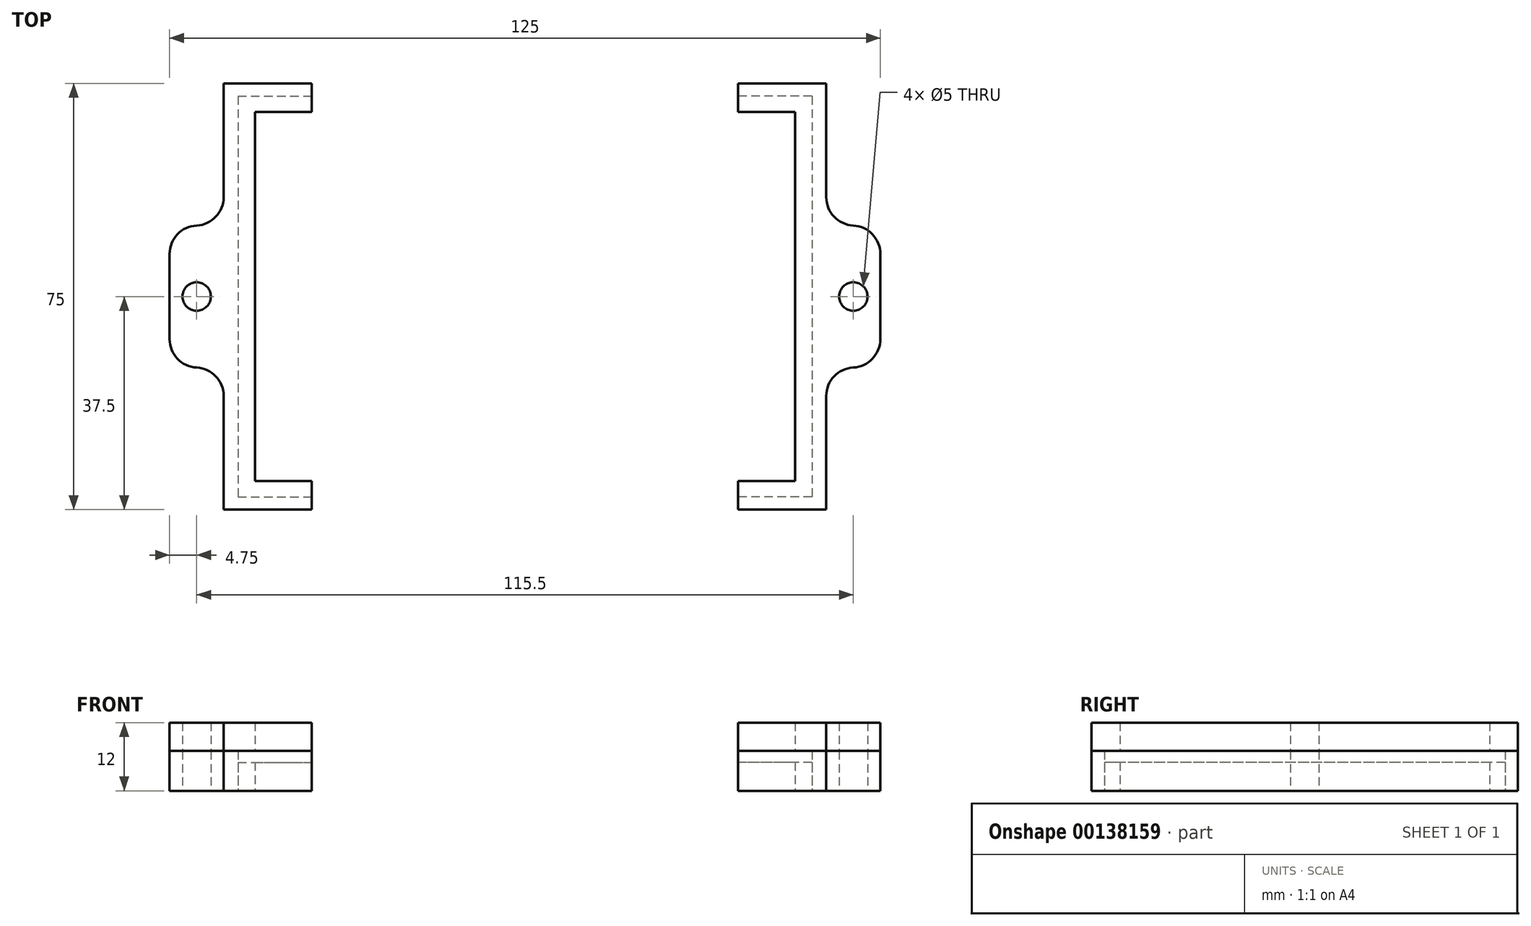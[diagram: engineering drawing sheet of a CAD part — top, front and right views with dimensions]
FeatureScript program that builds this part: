
annotation { "Feature Type Name" : "Feature", "Feature Type Description" : "" }
export const myFeature = defineFeature(function(context is Context, id is Id, definition is map)
    precondition{}
    {
        {
            var Q0;
            Q0=qCreatedBy(makeId("Top.planeOp"),FACE);
            var sketch = newSketch(context, id + "F0", { "sketchPlane" : qUnion([Q0])});
            skLineSegment(sketch, "E0.left", {"start": v(-50.5, 35.25) * mm, "end": v(-50.5, -35.25) * mm});
            skLineSegment(sketch, "E0.right", {"start": v(50.5, 35.25) * mm, "end": v(50.5, -35.25) * mm});
            skPoint(sketch, "E0.middle", {"position": v(0, 0) * mm});
            skLineSegment(sketch, "E1.left", {"start": v(-47.5, 32.5) * mm, "end": v(-47.5, -32.5) * mm});
            skLineSegment(sketch, "E1.right", {"start": v(47.5, 32.5) * mm, "end": v(47.5, -32.5) * mm});
            skLineSegment(sketch, "E2.left", {"start": v(-62.5, 12.5) * mm, "end": v(-62.5, -12.5) * mm});
            skLineSegment(sketch, "E2.right", {"start": v(62.5, 12.5) * mm, "end": v(62.5, -12.5) * mm});
            skPoint(sketch, "E3", {"position": v(-37.5, 37.5) * mm});
            skPoint(sketch, "E4", {"position": v(-37.5, 32.5) * mm});
            skPoint(sketch, "E5", {"position": v(37.5, 37.5) * mm});
            skPoint(sketch, "E6", {"position": v(37.5, 32.5) * mm});
            skPoint(sketch, "E7", {"position": v(37.5, -32.5) * mm});
            skPoint(sketch, "E8", {"position": v(37.5, -37.5) * mm});
            skPoint(sketch, "E9", {"position": v(-37.5, -37.5) * mm});
            skPoint(sketch, "E10", {"position": v(-37.5, -32.5) * mm});
            skPoint(sketch, "E11", {"position": v(-53, 12.5) * mm});
            skPoint(sketch, "E12", {"position": v(-53, -12.5) * mm});
            skPoint(sketch, "E13", {"position": v(53, 12.5) * mm});
            skPoint(sketch, "E14", {"position": v(53, -12.5) * mm});
            skLineSegment(sketch, "E15", {"start": v(-37.5, 37.5) * mm, "end": v(-37.5, 32.5) * mm});
            skLineSegment(sketch, "E16", {"start": v(37.5, 37.5) * mm, "end": v(37.5, 32.5) * mm});
            skLineSegment(sketch, "E17", {"start": v(37.5, -32.5) * mm, "end": v(37.5, -37.5) * mm});
            skLineSegment(sketch, "E18", {"start": v(-37.5, -32.5) * mm, "end": v(-37.5, -37.5) * mm});
            skLineSegment(sketch, "E19", {"start": v(-62.5, 12.5) * mm, "end": v(-53, 12.5) * mm});
            skLineSegment(sketch, "E20", {"start": v(-62.5, -12.5) * mm, "end": v(-53, -12.5) * mm});
            skLineSegment(sketch, "E21", {"start": v(62.5, 12.5) * mm, "end": v(53, 12.5) * mm});
            skLineSegment(sketch, "E22", {"start": v(62.5, -12.5) * mm, "end": v(53, -12.5) * mm});
            skLineSegment(sketch, "E23", {"start": v(47.5, 32.5) * mm, "end": v(37.5, 32.5) * mm});
            skLineSegment(sketch, "E24", {"start": v(53, 37.5) * mm, "end": v(37.5, 37.5) * mm});
            skLineSegment(sketch, "E25", {"start": v(-37.5, 32.5) * mm, "end": v(-47.5, 32.5) * mm});
            skLineSegment(sketch, "E26", {"start": v(-53, 37.5) * mm, "end": v(-37.5, 37.5) * mm});
            skLineSegment(sketch, "E27", {"start": v(-50.5, 35.25) * mm, "end": v(-37.5, 35.25) * mm});
            skLineSegment(sketch, "E28", {"start": v(50.5, 35.25) * mm, "end": v(37.5, 35.25) * mm});
            skLineSegment(sketch, "E29", {"start": v(-47.5, -32.5) * mm, "end": v(-37.5, -32.5) * mm});
            skLineSegment(sketch, "E30", {"start": v(-37.5, -37.5) * mm, "end": v(-53, -37.5) * mm});
            skLineSegment(sketch, "E31", {"start": v(37.5, -32.5) * mm, "end": v(47.5, -32.5) * mm});
            skLineSegment(sketch, "E32", {"start": v(37.5, -37.5) * mm, "end": v(53, -37.5) * mm});
            skLineSegment(sketch, "E33", {"start": v(50.5, -35.25) * mm, "end": v(37.5, -35.25) * mm});
            skLineSegment(sketch, "E34", {"start": v(-50.5, -35.25) * mm, "end": v(-37.5, -35.25) * mm});
            skLineSegment(sketch, "E35", {"start": v(-53, 37.5) * mm, "end": v(-53, 12.5) * mm});
            skLineSegment(sketch, "E36", {"start": v(-53, -12.5) * mm, "end": v(-53, -37.5) * mm});
            skLineSegment(sketch, "E37", {"start": v(53, -37.5) * mm, "end": v(53, -12.5) * mm});
            skLineSegment(sketch, "E38", {"start": v(53, 12.5) * mm, "end": v(53, 37.5) * mm});
            skLineSegment(sketch, "E39", {"start": v(-62.5, 12.5) * mm, "end": v(-53, -12.5) * mm, "construction": true});
            skLineSegment(sketch, "E40", {"start": v(-53, 12.5) * mm, "end": v(-62.5, -12.5) * mm, "construction": true});
            skLineSegment(sketch, "E41", {"start": v(53, 12.5) * mm, "end": v(62.5, -12.5) * mm, "construction": true});
            skLineSegment(sketch, "E42", {"start": v(62.5, 12.5) * mm, "end": v(53, -12.5) * mm, "construction": true});
            skPoint(sketch, "E43", {"position": v(-57.75, 0) * mm});
            skPoint(sketch, "E44", {"position": v(57.75, 0) * mm});
            skCircle(sketch, "E45", {"center": v(-57.75, 0) * mm, "radius": 2.5 * mm});
            skCircle(sketch, "E46", {"center": v(57.75, 0) * mm, "radius": 2.5 * mm});
            skSolve(sketch);
        }
        {
            var Q0;
            Q0=makeQuery(id+"F0.imprint","IMPRINT",FACE,{"disambiguationData":[TD([[makeQuery(id+"F0.imprint","IMPRINT",EDGE,{"derivedFrom":sQuery(id+"F0.wireOp",EDGE,"E0.left")}),1.0]])]});
            var Q1;
            Q1=makeQuery(id+"F0.imprint","IMPRINT",FACE,{"disambiguationData":[TD([[makeQuery(id+"F0.imprint","IMPRINT",EDGE,{"derivedFrom":sQuery(id+"F0.wireOp",EDGE,"E0.right")}),-1.0]])]});
            extrude(context, id + "F1", {"entities" : qUnion([Q0, Q1]), "depth" : 5 * mm});
        }
        {
            var Q0;
            Q0=makeQuery(id+"F0.imprint","IMPRINT",FACE,{"disambiguationData":[TD([[makeQuery(id+"F0.imprint","IMPRINT",EDGE,{"derivedFrom":sQuery(id+"F0.wireOp",EDGE,"E0.left")}),-1.0]])]});
            var Q1;
            Q1=makeQuery(id+"F0.imprint","IMPRINT",FACE,{"disambiguationData":[TD([[makeQuery(id+"F0.imprint","IMPRINT",EDGE,{"derivedFrom":sQuery(id+"F0.wireOp",EDGE,"E0.right")}),1.0]])]});
            extrude(context, id + "F2", {"entities" : qUnion([Q0, Q1]), "depth" : 7 * mm});
        }
        {
            var Q0;
            Q0=makeQuery(id+"F0.imprint","IMPRINT",FACE,{"disambiguationData":[TD([[makeQuery(id+"F0.imprint","IMPRINT",EDGE,{"derivedFrom":sQuery(id+"F0.wireOp",EDGE,"E0.left")}),-1.0]])]});
            var Q1;
            Q1=makeQuery(id+"F0.imprint","IMPRINT",FACE,{"disambiguationData":[TD([[makeQuery(id+"F0.imprint","IMPRINT",EDGE,{"derivedFrom":sQuery(id+"F0.wireOp",EDGE,"E0.left")}),1.0]])]});
            var Q2;
            Q2=makeQuery(id+"F0.imprint","IMPRINT",FACE,{"disambiguationData":[TD([[makeQuery(id+"F0.imprint","IMPRINT",EDGE,{"derivedFrom":sQuery(id+"F0.wireOp",EDGE,"E0.right")}),1.0]])]});
            var Q3;
            Q3=makeQuery(id+"F0.imprint","IMPRINT",FACE,{"disambiguationData":[TD([[makeQuery(id+"F0.imprint","IMPRINT",EDGE,{"derivedFrom":sQuery(id+"F0.wireOp",EDGE,"E0.right")}),-1.0]])]});
            extrude(context, id + "F3", {"entities" : qUnion([Q0, Q1, Q2, Q3]), "depth" : 12 * mm, "hasSecondDirection" : true, "secondDirectionOppositeDirection" : false, "secondDirectionDepth" : 7 * mm});
        }
        {
            var Q0;
            Q0=makeQuery(id+"F3.opExtrude","SWEPT_EDGE",EDGE,{"disambiguationData":[OSD([sQuery(id+"F0.wireOp",EDGE,"E2.left"),sQuery(id+"F0.wireOp",EDGE,"E20")])]});
            var Q1;
            Q1=makeQuery(id+"F2.opExtrude","SWEPT_EDGE",EDGE,{"disambiguationData":[OSD([sQuery(id+"F0.wireOp",EDGE,"E2.left"),sQuery(id+"F0.wireOp",EDGE,"E20")])]});
            var Q2;
            Q2=makeQuery(id+"F3.opExtrude","SWEPT_EDGE",EDGE,{"disambiguationData":[OSD([sQuery(id+"F0.wireOp",EDGE,"E2.right"),sQuery(id+"F0.wireOp",EDGE,"E22")])]});
            var Q3;
            Q3=makeQuery(id+"F2.opExtrude","SWEPT_EDGE",EDGE,{"disambiguationData":[OSD([sQuery(id+"F0.wireOp",EDGE,"E2.right"),sQuery(id+"F0.wireOp",EDGE,"E22")])]});
            var Q4;
            Q4=makeQuery(id+"F2.opExtrude","SWEPT_EDGE",EDGE,{"disambiguationData":[OSD([sQuery(id+"F0.wireOp",EDGE,"E2.right"),sQuery(id+"F0.wireOp",EDGE,"E21")])]});
            var Q5;
            Q5=makeQuery(id+"F3.opExtrude","SWEPT_EDGE",EDGE,{"disambiguationData":[OSD([sQuery(id+"F0.wireOp",EDGE,"E2.right"),sQuery(id+"F0.wireOp",EDGE,"E21")])]});
            var Q6;
            Q6=makeQuery(id+"F3.opExtrude","SWEPT_EDGE",EDGE,{"disambiguationData":[OSD([sQuery(id+"F0.wireOp",EDGE,"E2.left"),sQuery(id+"F0.wireOp",EDGE,"E19")])]});
            var Q7;
            Q7=makeQuery(id+"F2.opExtrude","SWEPT_EDGE",EDGE,{"disambiguationData":[OSD([sQuery(id+"F0.wireOp",EDGE,"E2.left"),sQuery(id+"F0.wireOp",EDGE,"E19")])]});
            fillet(context, id + "F4", {"entities" : qUnion([Q0, Q1, Q2, Q3, Q4, Q5, Q6, Q7]), "radius" : 5 * mm, "tangentPropagation" : true, "allowEdgeOverflow" : false});
        }
        {
            var Q0;
            Q0=makeQuery(id+"F2.opExtrude","SWEPT_EDGE",EDGE,{"disambiguationData":[OSD([sQuery(id+"F0.wireOp",EDGE,"E19"),sQuery(id+"F0.wireOp",EDGE,"E35")])]});
            var Q1;
            Q1=makeQuery(id+"F3.opExtrude","SWEPT_EDGE",EDGE,{"disambiguationData":[OSD([sQuery(id+"F0.wireOp",EDGE,"E19"),sQuery(id+"F0.wireOp",EDGE,"E35")])]});
            var Q2;
            Q2=makeQuery(id+"F2.opExtrude","SWEPT_EDGE",EDGE,{"disambiguationData":[OSD([sQuery(id+"F0.wireOp",EDGE,"E21"),sQuery(id+"F0.wireOp",EDGE,"E38")])]});
            var Q3;
            Q3=makeQuery(id+"F3.opExtrude","SWEPT_EDGE",EDGE,{"disambiguationData":[OSD([sQuery(id+"F0.wireOp",EDGE,"E21"),sQuery(id+"F0.wireOp",EDGE,"E38")])]});
            var Q4;
            Q4=makeQuery(id+"F2.opExtrude","SWEPT_EDGE",EDGE,{"disambiguationData":[OSD([sQuery(id+"F0.wireOp",EDGE,"E20"),sQuery(id+"F0.wireOp",EDGE,"E36")])]});
            var Q5;
            Q5=makeQuery(id+"F3.opExtrude","SWEPT_EDGE",EDGE,{"disambiguationData":[OSD([sQuery(id+"F0.wireOp",EDGE,"E20"),sQuery(id+"F0.wireOp",EDGE,"E36")])]});
            var Q6;
            Q6=makeQuery(id+"F2.opExtrude","SWEPT_EDGE",EDGE,{"disambiguationData":[OSD([sQuery(id+"F0.wireOp",EDGE,"E22"),sQuery(id+"F0.wireOp",EDGE,"E37")])]});
            var Q7;
            Q7=makeQuery(id+"F3.opExtrude","SWEPT_EDGE",EDGE,{"disambiguationData":[OSD([sQuery(id+"F0.wireOp",EDGE,"E22"),sQuery(id+"F0.wireOp",EDGE,"E37")])]});
            fillet(context, id + "F5", {"entities" : qUnion([Q0, Q1, Q2, Q3, Q4, Q5, Q6, Q7]), "radius" : 5 * mm, "tangentPropagation" : true, "allowEdgeOverflow" : false});
        }
    });
